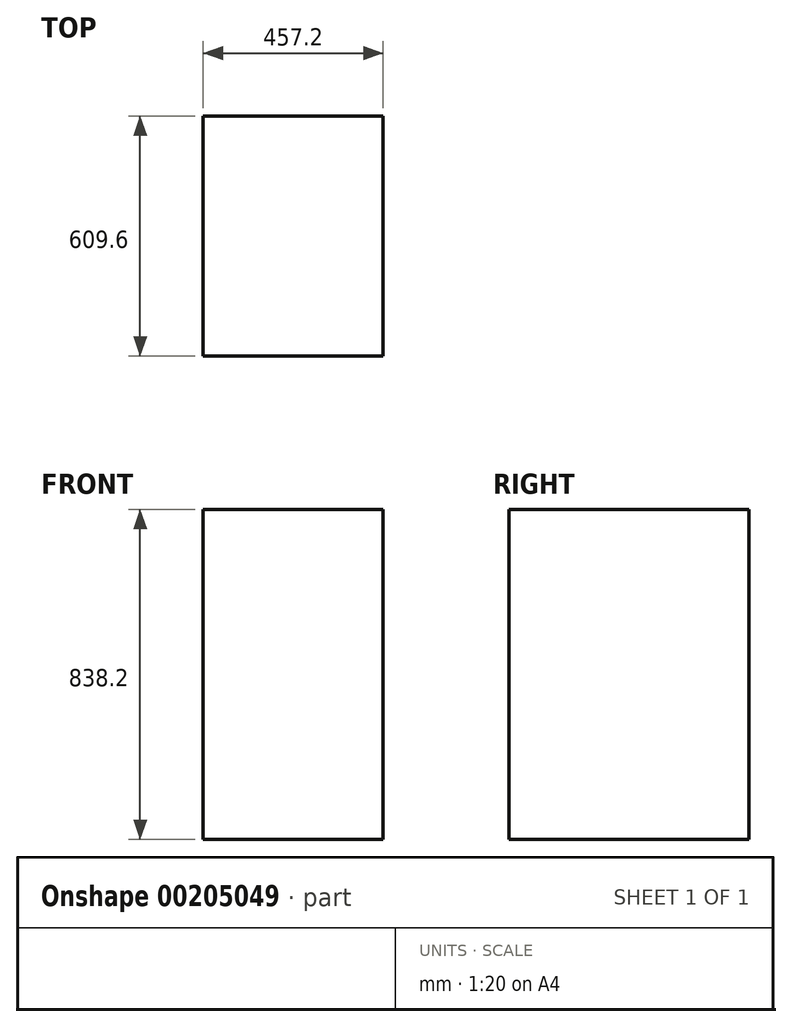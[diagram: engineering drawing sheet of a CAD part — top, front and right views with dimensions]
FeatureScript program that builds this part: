
annotation { "Feature Type Name" : "Feature", "Feature Type Description" : "" }
export const myFeature = defineFeature(function(context is Context, id is Id, definition is map)
    precondition{}
    {
        {
            var Q0;
            Q0=qCreatedBy(makeId("Top.planeOp"), FACE);
            var sketch = newSketch(context, id + "F0", { "sketchPlane" : qUnion([Q0])});
            skLineSegment(sketch, "E0.bottom", {"start": v(228.6, 304.8) * mm, "end": v(-228.6, 304.8) * mm});
            skLineSegment(sketch, "E0.top", {"start": v(228.6, -304.8) * mm, "end": v(-228.6, -304.8) * mm});
            skLineSegment(sketch, "E0.left", {"start": v(228.6, 304.8) * mm, "end": v(228.6, -304.8) * mm});
            skLineSegment(sketch, "E0.right", {"start": v(-228.6, 304.8) * mm, "end": v(-228.6, -304.8) * mm});
            skPoint(sketch, "E0.middle", {"position": v(0, 0) * mm});
            skSolve(sketch);
        }
        {
            var Q0;
            Q0 = qSketchRegion(id + "F0", true);
            var Q1;
            Q1 = qConstructionFilter(qBodyType(qCreatedBy(id + "F0" ,EDGE), BodyType.WIRE), ConstructionObject.NO);
            extrude(context, id + "F1", {"entities" : qUnion([Q0]), "surfaceEntities" : qUnion([Q1]), "depth" : 838.2 * mm, "offsetDistance" : 30.48 * mm});
        }
    });
